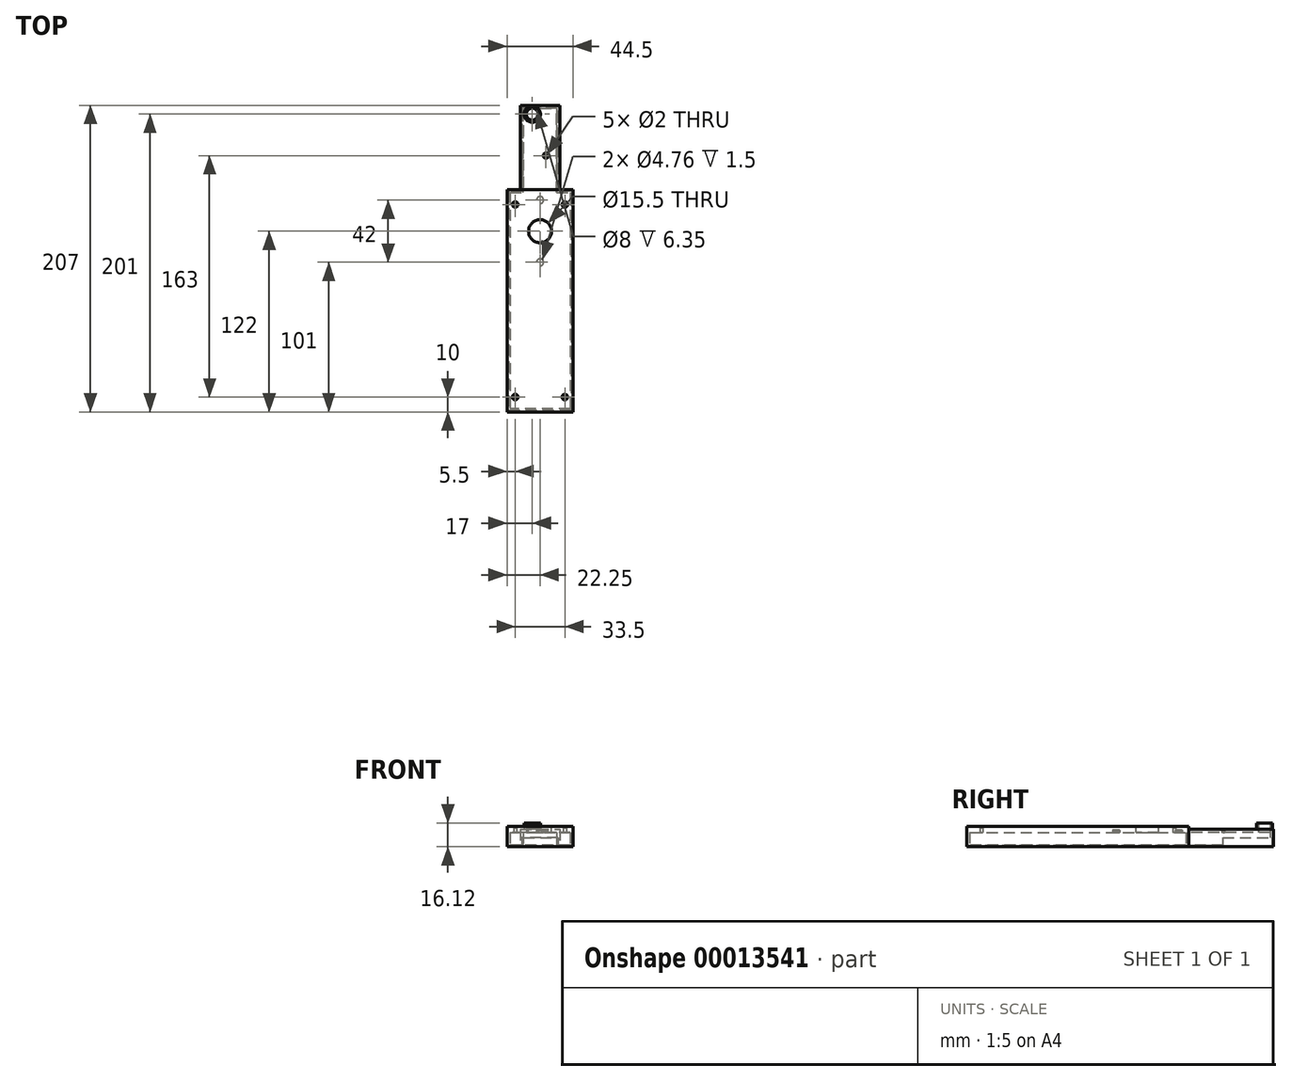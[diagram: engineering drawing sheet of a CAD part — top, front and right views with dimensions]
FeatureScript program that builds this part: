
annotation { "Feature Type Name" : "Feature", "Feature Type Description" : "" }
export const myFeature = defineFeature(function(context is Context, id is Id, definition is map)
    precondition{}
    {
        {
            var Q0;
            Q0=qCreatedBy(makeId("Top.planeOp"),FACE);
            var sketch = newSketch(context, id + "F0", { "sketchPlane" : qUnion([Q0])});
            skLineSegment(sketch, "E0.bottom", {"start": v(0, 0) * mm, "end": v(44.5, 0) * mm});
            skLineSegment(sketch, "E0.left", {"start": v(0, 0) * mm, "end": v(0, 150) * mm});
            skLineSegment(sketch, "E0.right", {"start": v(44.5, 0) * mm, "end": v(44.5, 150) * mm});
            skLineSegment(sketch, "E1", {"start": v(35.5, 150) * mm, "end": v(35.5, 207) * mm});
            skLineSegment(sketch, "E2", {"start": v(35.5, 207) * mm, "end": v(9, 207) * mm});
            skLineSegment(sketch, "E3", {"start": v(9, 207) * mm, "end": v(9, 150) * mm});
            skLineSegment(sketch, "E4", {"start": v(44.5, 150) * mm, "end": v(35.5, 150) * mm});
            skLineSegment(sketch, "E5", {"start": v(9, 150) * mm, "end": v(0, 150) * mm});
            skSolve(sketch);
        }
        {
            var Q0;
            Q0 = qSketchRegion(id + "F0", true);
            extrude(context, id + "F1", {"entities" : qUnion([Q0]), "depth" : 11.77 * mm});
        }
        {
            var Q0;
            Q0=makeQuery(id+"F1.opExtrude","CAP_FACE",FACE,{"disambiguationData":[OSD([sQuery(id+"F0.wireOp",EDGE,"E0.bottom"),sQuery(id+"F0.wireOp",EDGE,"E0.left"),sQuery(id+"F0.wireOp",EDGE,"E0.right"),sQuery(id+"F0.wireOp",EDGE,"E1"),sQuery(id+"F0.wireOp",EDGE,"E2"),sQuery(id+"F0.wireOp",EDGE,"E3"),sQuery(id+"F0.wireOp",EDGE,"E4"),sQuery(id+"F0.wireOp",EDGE,"E5")])],"isStart":true});
            shell(context, id + "F2", {"entities" : qUnion([Q0]), "thickness" : 2 * mm});
        }
        {
            var Q0;
            Q0=makeQuery(id+"F1.opExtrude","CAP_FACE",FACE,{"disambiguationData":[OSD([sQuery(id+"F0.wireOp",EDGE,"E0.bottom"),sQuery(id+"F0.wireOp",EDGE,"E0.left"),sQuery(id+"F0.wireOp",EDGE,"E0.right"),sQuery(id+"F0.wireOp",EDGE,"E1"),sQuery(id+"F0.wireOp",EDGE,"E2"),sQuery(id+"F0.wireOp",EDGE,"E3"),sQuery(id+"F0.wireOp",EDGE,"E4"),sQuery(id+"F0.wireOp",EDGE,"E5")])],"isStart":true});
            var sketch = newSketch(context, id + "F3", { "sketchPlane" : qUnion([Q0])});
            skLineSegment(sketch, "E6", {"start": v(34.5, -206) * mm, "end": v(10, -206) * mm});
            skLineSegment(sketch, "E7", {"start": v(10, -206) * mm, "end": v(10, -149) * mm});
            skLineSegment(sketch, "E8", {"start": v(10, -149) * mm, "end": v(1, -149) * mm});
            skLineSegment(sketch, "E9", {"start": v(1, -149) * mm, "end": v(1, -1) * mm});
            skLineSegment(sketch, "E10", {"start": v(1, -1) * mm, "end": v(43.5, -1) * mm});
            skLineSegment(sketch, "E11", {"start": v(43.5, -1) * mm, "end": v(43.5, -149) * mm});
            skLineSegment(sketch, "E12", {"start": v(43.5, -149) * mm, "end": v(34.5, -149) * mm});
            skLineSegment(sketch, "E13", {"start": v(34.5, -149) * mm, "end": v(34.5, -206) * mm});
            skSolve(sketch);
        }
        {
            var Q0;
            Q0 = qSketchRegion(id + "F3", true);
            extrude(context, id + "F4", {"entities" : qUnion([Q0]), "operationType" : NewBodyOperationType.REMOVE, "oppositeDirection" : true, "depth" : 1 * mm});
        }
        {
            var Q0;
            Q0=makeQuery(id+"F1.opExtrude","CAP_FACE",FACE,{"disambiguationData":[OSD([sQuery(id+"F0.wireOp",EDGE,"E0.bottom"),sQuery(id+"F0.wireOp",EDGE,"E0.left"),sQuery(id+"F0.wireOp",EDGE,"E0.right"),sQuery(id+"F0.wireOp",EDGE,"E1"),sQuery(id+"F0.wireOp",EDGE,"E2"),sQuery(id+"F0.wireOp",EDGE,"E3"),sQuery(id+"F0.wireOp",EDGE,"E4"),sQuery(id+"F0.wireOp",EDGE,"E5")])],"isStart":false});
            var sketch = newSketch(context, id + "F5", { "sketchPlane" : qUnion([Q0])});
            skCircle(sketch, "E14", {"center": v(22.25, 122) * mm, "radius": 7.75 * mm});
            skLineSegment(sketch, "E15", {"start": v(22.25, 207) * mm, "end": v(22.25, 61.27) * mm, "construction": true});
            skSolve(sketch);
        }
        {
            var Q0;
            Q0 = qSketchRegion(id + "F5", true);
            var Q1;
            Q1=makeQuery(id+"F2.opShell","OFFSET_FACE",FACE,{"disambiguationData":[OSD([sQuery(id+"F0.wireOp",EDGE,"E0.bottom"),sQuery(id+"F0.wireOp",EDGE,"E0.left"),sQuery(id+"F0.wireOp",EDGE,"E0.right"),sQuery(id+"F0.wireOp",EDGE,"E1"),sQuery(id+"F0.wireOp",EDGE,"E2"),sQuery(id+"F0.wireOp",EDGE,"E3"),sQuery(id+"F0.wireOp",EDGE,"E4"),sQuery(id+"F0.wireOp",EDGE,"E5")])]});
            extrude(context, id + "F6", {"entities" : qUnion([Q0]), "operationType" : NewBodyOperationType.REMOVE, "endBound" : BoundingType.UP_TO_SURFACE, "oppositeDirection" : true, "endBoundEntityFace" : qUnion([Q1]), "depth" : 25 * mm});
        }
        {
            var Q0;
            Q0=makeQuery(id+"F1.opExtrude","CAP_FACE",FACE,{"disambiguationData":[OSD([sQuery(id+"F0.wireOp",EDGE,"E0.bottom"),sQuery(id+"F0.wireOp",EDGE,"E0.left"),sQuery(id+"F0.wireOp",EDGE,"E0.right"),sQuery(id+"F0.wireOp",EDGE,"E1"),sQuery(id+"F0.wireOp",EDGE,"E2"),sQuery(id+"F0.wireOp",EDGE,"E3"),sQuery(id+"F0.wireOp",EDGE,"E4"),sQuery(id+"F0.wireOp",EDGE,"E5")])],"isStart":false});
            var sketch = newSketch(context, id + "F7", { "sketchPlane" : qUnion([Q0])});
            skLineSegment(sketch, "E16.bottom", {"start": v(0, 150) * mm, "end": v(44.5, 150) * mm});
            skLineSegment(sketch, "E16.top", {"start": v(0, 0) * mm, "end": v(44.5, 0) * mm});
            skLineSegment(sketch, "E16.left", {"start": v(0, 150) * mm, "end": v(0, 0) * mm});
            skLineSegment(sketch, "E16.right", {"start": v(44.5, 150) * mm, "end": v(44.5, 0) * mm});
            skCircle(sketch, "E17", {"center": v(22.25, 122) * mm, "radius": 7.75 * mm});
            skSolve(sketch);
        }
        {
            var Q0;
            Q0 = qSketchRegion(id + "F7", true);
            extrude(context, id + "F8", {"entities" : qUnion([Q0]), "operationType" : NewBodyOperationType.ADD, "depth" : 2 * mm});
        }
        {
            var Q0;
            Q0=makeQuery(id+"F8.opExtrude","CAP_FACE",FACE,{"disambiguationData":[OSD([sQuery(id+"F7.wireOp",EDGE,"E16.bottom"),sQuery(id+"F7.wireOp",EDGE,"E16.top"),sQuery(id+"F7.wireOp",EDGE,"E16.left"),sQuery(id+"F7.wireOp",EDGE,"E16.right"),sQuery(id+"F7.wireOp",EDGE,"E17")])],"isStart":false});
            var sketch = newSketch(context, id + "F9", { "sketchPlane" : qUnion([Q0])});
            skLineSegment(sketch, "E18", {"start": v(39, 149) * mm, "end": v(39, 0) * mm, "construction": true});
            skLineSegment(sketch, "E19", {"start": v(44.5, 140) * mm, "end": v(0, 140) * mm, "construction": true});
            skLineSegment(sketch, "E20", {"start": v(5.5, 149) * mm, "end": v(5.5, 0) * mm, "construction": true});
            skLineSegment(sketch, "E21", {"start": v(0, 10) * mm, "end": v(44.5, 10) * mm, "construction": true});
            skLineSegment(sketch, "E22", {"start": v(22.25, 207) * mm, "end": v(22.25, 0) * mm, "construction": true});
            skPoint(sketch, "E23", {"position": v(5.5, 140) * mm});
            skPoint(sketch, "E24", {"position": v(39, 140) * mm});
            skPoint(sketch, "E25", {"position": v(5.5, 10) * mm});
            skPoint(sketch, "E26", {"position": v(39, 10) * mm});
            skLineSegment(sketch, "E27", {"start": v(43.5, 149) * mm, "end": v(34.5, 149) * mm, "construction": true});
            skLineSegment(sketch, "E28", {"start": v(1, 149) * mm, "end": v(10, 149) * mm, "construction": true});
            skSolve(sketch);
        }
        {
            var Q0;
            Q0=sQuery(id+"F9.wireOp",VERTEX,"E23");
            var Q1;
            Q1=sQuery(id+"F9.wireOp",VERTEX,"E24");
            var Q2;
            Q2=sQuery(id+"F9.wireOp",VERTEX,"E25");
            var Q3;
            Q3=sQuery(id+"F9.wireOp",VERTEX,"E26");
            var Q4;
            Q4=makeQuery(id+"F1.opExtrude","SWEPT_BODY",BODY,{"disambiguationData":[OSD([sQuery(id+"F0.wireOp",EDGE,"E0.bottom"),sQuery(id+"F0.wireOp",EDGE,"E0.left"),sQuery(id+"F0.wireOp",EDGE,"E0.right"),sQuery(id+"F0.wireOp",EDGE,"E1"),sQuery(id+"F0.wireOp",EDGE,"E2"),sQuery(id+"F0.wireOp",EDGE,"E3"),sQuery(id+"F0.wireOp",EDGE,"E4"),sQuery(id+"F0.wireOp",EDGE,"E5")])]});
            hole(context, id + "F10", {"style" : HoleStyle.C_SINK, "holeDiameter" : 2 * mm, "cSinkDiameter" : 3.8 * mm, "endStyle" : HoleEndStyle.THROUGH, "locations" : qUnion([Q0, Q1, Q2, Q3]), "scope" : qUnion([Q4]), "cSinkAngle" : 90 * degree});
        }
        {
            var Q0;
            Q0=makeQuery(id+"F1.opExtrude","CAP_FACE",FACE,{"disambiguationData":[OSD([sQuery(id+"F0.wireOp",EDGE,"E0.bottom"),sQuery(id+"F0.wireOp",EDGE,"E0.left"),sQuery(id+"F0.wireOp",EDGE,"E0.right"),sQuery(id+"F0.wireOp",EDGE,"E1"),sQuery(id+"F0.wireOp",EDGE,"E2"),sQuery(id+"F0.wireOp",EDGE,"E3"),sQuery(id+"F0.wireOp",EDGE,"E4"),sQuery(id+"F0.wireOp",EDGE,"E5")])],"isStart":false});
            var sketch = newSketch(context, id + "F11", { "sketchPlane" : qUnion([Q0])});
            skLineSegment(sketch, "E29", {"start": v(22.25, 207) * mm, "end": v(22.25, 150) * mm, "construction": true});
            skPoint(sketch, "E30", {"position": v(26.25, 173) * mm});
            skSolve(sketch);
        }
        {
            var Q0;
            Q0=sQuery(id+"F11.wireOp",VERTEX,"E30");
            var Q1;
            Q1=makeQuery(id+"F1.opExtrude","SWEPT_BODY",BODY,{"disambiguationData":[OSD([sQuery(id+"F0.wireOp",EDGE,"E0.bottom"),sQuery(id+"F0.wireOp",EDGE,"E0.left"),sQuery(id+"F0.wireOp",EDGE,"E0.right"),sQuery(id+"F0.wireOp",EDGE,"E1"),sQuery(id+"F0.wireOp",EDGE,"E2"),sQuery(id+"F0.wireOp",EDGE,"E3"),sQuery(id+"F0.wireOp",EDGE,"E4"),sQuery(id+"F0.wireOp",EDGE,"E5")])]});
            hole(context, id + "F12", {"style" : HoleStyle.C_SINK, "holeDiameter" : 2 * mm, "cSinkDiameter" : 3.6 * mm, "endStyle" : HoleEndStyle.THROUGH, "locations" : qUnion([Q0]), "scope" : qUnion([Q1]), "cSinkAngle" : 90 * degree});
        }
        {
            var Q0;
            Q0=makeQuery(id+"F2.opShell","OFFSET_FACE",FACE,{"disambiguationData":[OSD([sQuery(id+"F0.wireOp",EDGE,"E0.bottom"),sQuery(id+"F0.wireOp",EDGE,"E0.left"),sQuery(id+"F0.wireOp",EDGE,"E0.right"),sQuery(id+"F0.wireOp",EDGE,"E1"),sQuery(id+"F0.wireOp",EDGE,"E2"),sQuery(id+"F0.wireOp",EDGE,"E3"),sQuery(id+"F0.wireOp",EDGE,"E4"),sQuery(id+"F0.wireOp",EDGE,"E5")])]});
            var sketch = newSketch(context, id + "F13", { "sketchPlane" : qUnion([Q0])});
            skCircle(sketch, "E31", {"center": v(22.25, -143) * mm, "radius": 2.38 * mm});
            skCircle(sketch, "E32", {"center": v(22.25, -101) * mm, "radius": 2.38 * mm});
            skLineSegment(sketch, "E33", {"start": v(22.25, -122) * mm, "end": v(22.25, -207) * mm, "construction": true});
            skLineSegment(sketch, "E34", {"start": v(22.25, -122) * mm, "end": v(22.25, 0) * mm, "construction": true});
            skLineSegment(sketch, "E35", {"start": v(22.25, -143) * mm, "end": v(22.25, -122) * mm, "construction": true});
            skLineSegment(sketch, "E36", {"start": v(22.25, -122) * mm, "end": v(22.25, -101) * mm, "construction": true});
            skSolve(sketch);
        }
        {
            var Q0;
            Q0 = qSketchRegion(id + "F13", true);
            extrude(context, id + "F14", {"entities" : qUnion([Q0]), "operationType" : NewBodyOperationType.REMOVE, "oppositeDirection" : true, "depth" : 1.5 * mm});
        }
        {
            var Q0;
            Q0=makeQuery(id+"F4.boolean.opBoolean","COPY",FACE,{"derivedFrom":makeQuery(id+"F4.opExtrude","CAP_FACE",FACE,{"disambiguationData":[OSD([sQuery(id+"F3.wireOp",EDGE,"E6"),sQuery(id+"F3.wireOp",EDGE,"E7"),sQuery(id+"F3.wireOp",EDGE,"E8"),sQuery(id+"F3.wireOp",EDGE,"E9"),sQuery(id+"F3.wireOp",EDGE,"E10"),sQuery(id+"F3.wireOp",EDGE,"E11"),sQuery(id+"F3.wireOp",EDGE,"E12"),sQuery(id+"F3.wireOp",EDGE,"E13")])],"isStart":false})});
            var sketch = newSketch(context, id + "F15", { "sketchPlane" : qUnion([Q0])});
            skLineSegment(sketch, "E37.bottom", {"start": v(10, -206) * mm, "end": v(34.5, -206) * mm});
            skLineSegment(sketch, "E37.top", {"start": v(10, -173) * mm, "end": v(34.5, -173) * mm});
            skLineSegment(sketch, "E37.left", {"start": v(10, -206) * mm, "end": v(10, -173) * mm});
            skLineSegment(sketch, "E37.right", {"start": v(34.5, -206) * mm, "end": v(34.5, -173) * mm});
            skSolve(sketch);
        }
        {
            var Q0;
            Q0 = qSketchRegion(id + "F15", true);
            extrude(context, id + "F16", {"entities" : qUnion([Q0]), "operationType" : NewBodyOperationType.REMOVE, "oppositeDirection" : true, "depth" : 5 * mm});
        }
        {
            var Q0;
            Q0=makeQuery(id+"F2.opShell","OFFSET_FACE",FACE,{"disambiguationData":[OSD([sQuery(id+"F0.wireOp",EDGE,"E0.bottom"),sQuery(id+"F0.wireOp",EDGE,"E0.left"),sQuery(id+"F0.wireOp",EDGE,"E0.right"),sQuery(id+"F0.wireOp",EDGE,"E1"),sQuery(id+"F0.wireOp",EDGE,"E2"),sQuery(id+"F0.wireOp",EDGE,"E3"),sQuery(id+"F0.wireOp",EDGE,"E4"),sQuery(id+"F0.wireOp",EDGE,"E5")])]});
            var sketch = newSketch(context, id + "F17", { "sketchPlane" : qUnion([Q0])});
            skCircle(sketch, "E38", {"center": v(17, -201) * mm, "radius": 4 * mm});
            skSolve(sketch);
        }
        {
            var Q0;
            Q0 = qSketchRegion(id + "F17", true);
            extrude(context, id + "F18", {"entities" : qUnion([Q0]), "operationType" : NewBodyOperationType.REMOVE, "endBound" : BoundingType.THROUGH_ALL, "oppositeDirection" : true, "depth" : 25 * mm});
        }
        {
            var Q0;
            Q0=makeQuery(id+"F1.opExtrude","CAP_FACE",FACE,{"disambiguationData":[OSD([sQuery(id+"F0.wireOp",EDGE,"E0.bottom"),sQuery(id+"F0.wireOp",EDGE,"E0.left"),sQuery(id+"F0.wireOp",EDGE,"E0.right"),sQuery(id+"F0.wireOp",EDGE,"E1"),sQuery(id+"F0.wireOp",EDGE,"E2"),sQuery(id+"F0.wireOp",EDGE,"E3"),sQuery(id+"F0.wireOp",EDGE,"E4"),sQuery(id+"F0.wireOp",EDGE,"E5")])],"isStart":false});
            var sketch = newSketch(context, id + "F19", { "sketchPlane" : qUnion([Q0])});
            skCircle(sketch, "E39", {"center": v(17, 201) * mm, "radius": 4 * mm});
            skCircle(sketch, "E40", {"center": v(17, 201) * mm, "radius": 5.5 * mm});
            skSolve(sketch);
        }
        {
            var Q0;
            Q0 = qSketchRegion(id + "F19", true);
            extrude(context, id + "F20", {"entities" : qUnion([Q0]), "operationType" : NewBodyOperationType.ADD, "depth" : 4.35 * mm});
        }
    });
